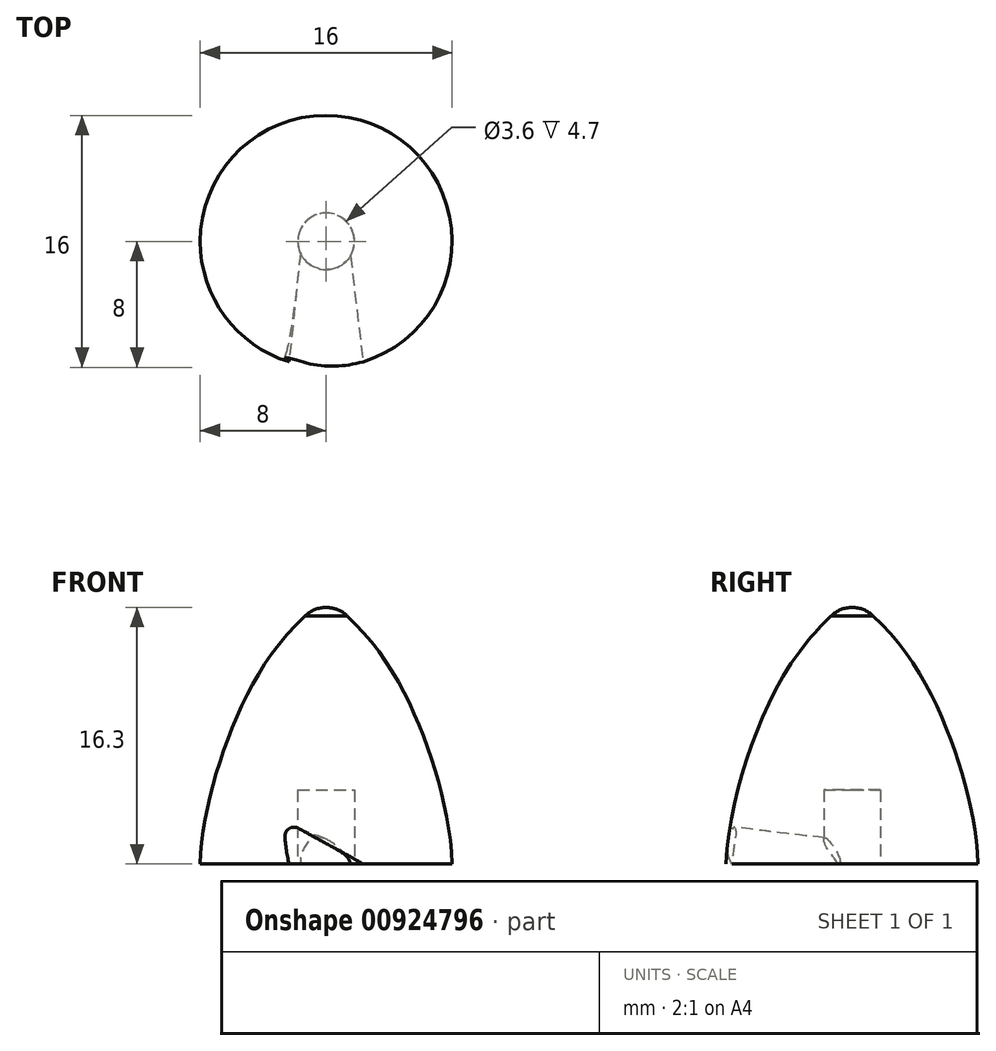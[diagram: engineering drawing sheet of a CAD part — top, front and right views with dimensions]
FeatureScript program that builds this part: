
annotation { "Feature Type Name" : "Feature", "Feature Type Description" : "" }
export const myFeature = defineFeature(function(context is Context, id is Id, definition is map)
    precondition{}
    {
        {
            var Q0;
            Q0=qCreatedBy(makeId("Front.planeOp"),FACE);
            var sketch = newSketch(context, id + "F0", { "sketchPlane" : qUnion([Q0])});
            skFitSpline(sketch, "E0", {"points": [v(-8, 0) * mm, v(-5.92, 8.78) * mm, v(0, 16.92) * mm], "startDerivative": vector(0.53, 17) * mm, "endDerivative": vector(17.9, 14.1) * mm});
            skLineSegment(sketch, "E1", {"start": v(-8, 0) * mm, "end": v(0, 0) * mm});
            skLineSegment(sketch, "E2", {"start": v(0, 0) * mm, "end": v(0, 16.3) * mm});
            skArc(sketch, "E3", {"start": v(0, 16.3) * mm, "mid": v(-0.72, 16.16) * mm, "end": v(-1.33, 15.77) * mm});
            skSolve(sketch);
        }
        {
            var Q0;
            Q0=makeQuery(id+"F0.imprint","IMPRINT",FACE,{"disambiguationData":[TD([[makeQuery(id+"F0.imprint","IMPRINT",EDGE,{"derivedFrom":sQuery(id+"F0.wireOp",EDGE,"E0")}),-1.0]])]});
            var Q1;
            Q1=sQuery(id+"F0.wireOp",EDGE,"E2");
            revolve(context, id + "F1", {"surfaceOperationType" : NewSurfaceOperationType.NEW, "entities" : qUnion([Q0]), "axis" : qUnion([Q1]), "revolveType" : RevolveType.FULL});
        }
        {
            var Q0;
            Q0=makeQuery(id+"F1.opRevolve","SWEPT_FACE",FACE,{"disambiguationData":[OSD([sQuery(id+"F0.wireOp",EDGE,"E1")])]});
            var sketch = newSketch(context, id + "F2", { "sketchPlane" : qUnion([Q0])});
            skCircle(sketch, "E4", {"center": v(0, 0) * mm, "radius": 1.8 * mm});
            skSolve(sketch);
        }
        {
            var Q0;
            Q0=makeQuery(id+"F2.imprint","IMPRINT",FACE,{"disambiguationData":[TD([[makeQuery(id+"F2.imprint","IMPRINT",EDGE,{"derivedFrom":sQuery(id+"F2.wireOp",EDGE,"E4")}),1.0]])]});
            extrude(context, id + "F3", {"entities" : qUnion([Q0]), "operationType" : NewBodyOperationType.REMOVE, "oppositeDirection" : true, "depth" : 4.7 * mm, "offsetDistance" : 25 * mm});
        }
        {
            var Q0;
            Q0=qCreatedBy(makeId("Front.planeOp"),FACE);
            cPlane(context, id + "F4", {"entities" : qUnion([Q0]), "cplaneType" : CPlaneType.OFFSET, "offset" : 9 * mm, "width" : 150 * mm, "height" : 150 * mm});
        }
        {
            var Q0;
            Q0=qCreatedBy(id+"F4.planeOp",FACE);
            var sketch = newSketch(context, id + "F5", { "sketchPlane" : qUnion([Q0])});
            skLineSegment(sketch, "E5", {"start": v(-2.5, 0) * mm, "end": v(-3, 1.91) * mm});
            skLineSegment(sketch, "E6", {"start": v(-2.29, 2.48) * mm, "end": v(2.5, 0) * mm});
            skLineSegment(sketch, "E7", {"start": v(2.5, 0) * mm, "end": v(-2.5, 0) * mm});
            skPoint(sketch, "E8.visualSharp", {"position": v(-3.28, 3) * mm});
            skArc(sketch, "E8.filletArc", {"start": v(-2.29, 2.48) * mm, "mid": v(-2.83, 2.43) * mm, "end": v(-3, 1.91) * mm});
            skSolve(sketch);
        }
        {
            var Q0;
            Q0=qCreatedBy(makeId("Front.planeOp"),FACE);
            var sketch = newSketch(context, id + "F6", { "sketchPlane" : qUnion([Q0])});
            skArc(sketch, "E9", {"start": v(1.45, 0) * mm, "mid": v(-0.05, 1.5) * mm, "end": v(-1.55, 0) * mm});
            skLineSegment(sketch, "E10", {"start": v(-1.55, 0) * mm, "end": v(1.45, 0) * mm});
            skSolve(sketch);
        }
        {
            var Q1;
            Q1=makeQuery(id+"F6.imprint","IMPRINT",FACE,{"disambiguationData":[TD([[makeQuery(id+"F6.imprint","IMPRINT",EDGE,{"derivedFrom":sQuery(id+"F6.wireOp",EDGE,"E9")}),1.0]])]});
            var Q2;
            Q2=makeQuery(id+"F5.imprint","IMPRINT",FACE,{"disambiguationData":[TD([[makeQuery(id+"F5.imprint","IMPRINT",EDGE,{"derivedFrom":sQuery(id+"F5.wireOp",EDGE,"E7")}),-1.0]])]});
            loft(context, id + "F7", {"operationType" : NewBodyOperationType.REMOVE, "sheetProfilesArray" : [{ "sheetProfileEntities" : qUnion([Q1]) }, { "sheetProfileEntities" : qUnion([Q2]) }]});
        }
    });
